# Revit family: Combina D 1.0
name_source: partatom
category: Lighting Fixtures
units: mm (PartAtom-declared; Revit-internal decimal feet)

## family parameters
Cut with Voids When Loaded = Yes
Host = Face
Light Source = Yes
Part Type = Normal
Room Calculation Point = Yes
Round Connector Dimension = Use Diameter
Shared = No

## types (12) — shared parameters
Apparent Load = 0 VA
Apparent Load Phase 1 = 6 W
Body = L&L_Anodized aluminium
CRI = CRI >90
Code = -
Color Filter = 16777215
Control system = ON/OFF
Cutout dimensions = diam. 70 mm
Default Elevation = 1219 mm
Delivered lumen output = 345 lm (3000K, 500mA, 16°)
Description = Recessed downlight for indoor applications
Dimming Lamp Color Temperature Shift = <None>
Emit from Line Length = 610 mm
Energy efficiency class = A A+ A++
Features = UGR <13 for versions with flat and shallow covers, UGR <19 for versions with deep cover
Geometry = Combina D 1.0_mod
Height Void = 88 mm  [stored 0.288714 ft]
Height mm = 87 mm  [stored 0.285433 ft]
IP = IP40, IP44 with filter
LED Colour = 3000K (also available: 2700K and 4000K - ref. URL Technical sheet)
Length mm = 70 mm  [stored 0.229659 ft]
Lens = L&L_Tempered extra-clear glass
Lumen output at source = 637 lm (3000K, 500mA)
Manufacturer = L&L Luce&Light
Material = body in die-cast aluminium and Bayblend, bezel and cover in die-cast aluminium
Model = Combina D 1.0
Mounting = recessed (ceiling)
No. and type of led = 1 power LED High Intensity, 3-step MacAdam, 50 000h L90 B10 (Ta 25°C)
Notes = -
Power = max 6W
Power cables = includes 2x0.30 m single-core PVC cables
Power supply = max 500mA
max 500mA
max 500mA
Power supply unit = not included
Radius Void = 50 mm  [stored 0.164042 ft]
Tilt Angle = 90.00°
Tiltable = -
Trim = L&L _Aluminium low copper
URL = https://www.lucelight.it
URL Accessories and power supply units = https://www.lucelight.it
URL Catalogue = https://www.lucelight.it
URL DXF = https://www.lucelight.it
URL Description = https://www.lucelight.it
URL General code = https://www.lucelight.it
URL IES Photometric file = https://www.lucelight.it
URL Image = https://www.lucelight.it
Voltage = 500 V
Weight kg = 0.30 kg
Width mm = 70 mm  [stored 0.229659 ft]
Wiring = series

## per-type parameters (varying)
| type | Optics | Photometric Web File | Round Deep | Round Flat | Square Deep | Square Flat |
| COMBINA D 1.0 + CC1010 S 16° (3000K 6W 500mA)_Round Flat | 16° | COMBINA D 1.0 + CC1010 S 16° [3000K 6W 500mA].IES | No | Yes | No | No |
| COMBINA D 1.0 + CC1020 S 16° (3000K 6W 500mA)_Square Flat | 16° | COMBINA D 1.0 + CC1020 S 16° [3000K 6W 500mA].IES | No | No | No | Yes |
| COMBINA D 1.0 + CC1050 S 16° (3000K 6W 500mA)_Round Deep | 16° | COMBINA D 1.0 + CC1050 S 16° [3000K 6W 500mA].IES | Yes | No | No | No |
| COMBINA D 1.0 + CC1060 S 16° (3000K 6W 500mA)_Square Deep | 16° | COMBINA D 1.0 + CC1060 S 16° [3000K 6W 500mA].IES | No | No | Yes | No |
| COMBINA D 1.0 + CC1010 M 22° (3000K 6W 500mA)_Round Flat | 22° | COMBINA D 1.0 + CC1010 M 22° [3000K 6W 500mA].IES | No | Yes | No | No |
| COMBINA D 1.0 + CC1020 M 22° (3000K 6W 500mA)_Square Flat | 22° | COMBINA D 1.0 + CC1020 M 22° [3000K 6W 500mA].IES | No | No | No | Yes |
| COMBINA D 1.0 + CC1050 M 23° (3000K 6W 500mA)_Round Deep | 23° | COMBINA D 1.0 + CC1050 M 23° [3000K 6W 500mA].IES | Yes | No | No | No |
| COMBINA D 1.0 + CC1060 M 23° (3000K 6W 500mA)_Square Deep | 23° | COMBINA D 1.0 + CC1060 M 23° [3000K 6W 500mA].IES | No | No | Yes | No |
| COMBINA D 1.0 + CC1010 L 33° (3000K 6W 500mA)_Round Flat | 33° | COMBINA D 1.0 + CC1010 L 33° [3000K 6W 500mA].IES | No | Yes | No | No |
| COMBINA D 1.0 + CC1020 L 33° (3000K 6W 500mA)_Square Flat | 33° | COMBINA D 1.0 + CC1020 L 33° [3000K 6W 500mA].IES | No | No | No | Yes |
| COMBINA D 1.0 + CC1060 L 42° (3000K 6W 500mA)_Square Deep | 42° | COMBINA D 1.0 + CC1060 L 42° [3000K 6W 500mA].IES | No | No | Yes | No |
| COMBINA D 1.0 + CC1050 L 42° (3000K 6W 500mA)_Round Deep | 42° | COMBINA D 1.0 + CC1050 L 42° [3000K 6W 500mA].IES | Yes | No | No | No |

note: [stored X ft] marks values corroborated as IEEE doubles in the binary element streams (Revit-internal decimal feet)

## geometry (parser evidence)
native form markers: Blend x2, Sweep x4
no freeform markers — native parametric forms only
